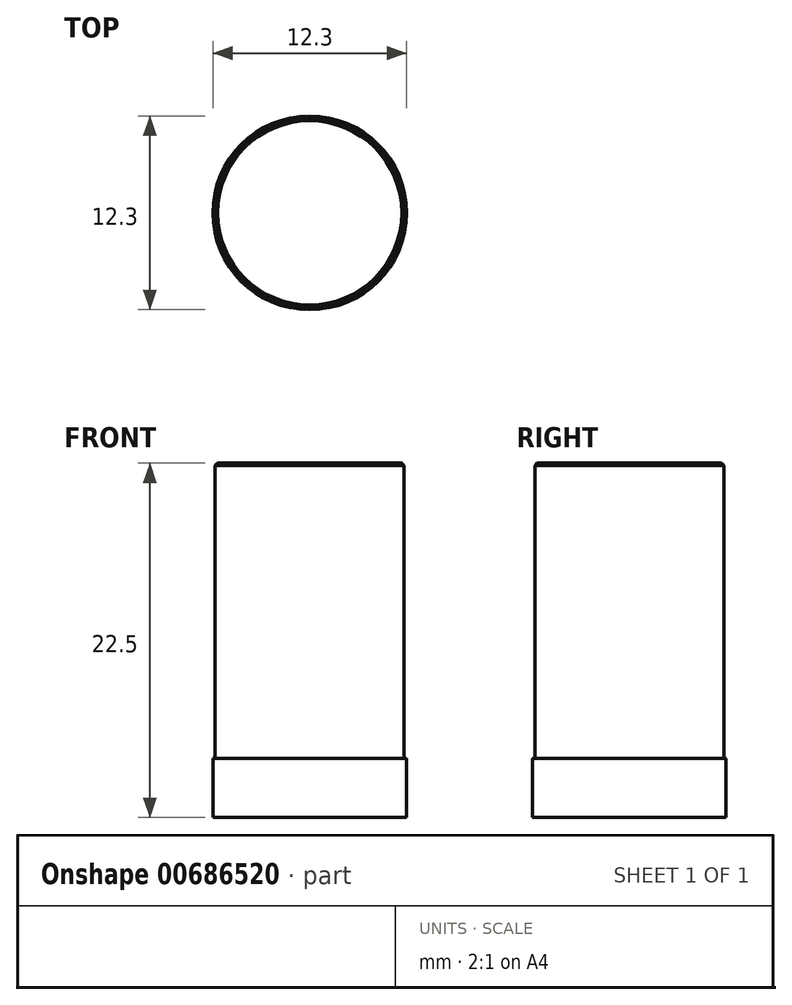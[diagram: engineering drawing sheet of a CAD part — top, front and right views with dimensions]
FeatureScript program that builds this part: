
annotation { "Feature Type Name" : "Feature", "Feature Type Description" : "" }
export const myFeature = defineFeature(function(context is Context, id is Id, definition is map)
    precondition{}
    {
        {
            var Q0;
            Q0=qCreatedBy(makeId("Top.planeOp"),FACE);
            var sketch = newSketch(context, id + "F0", { "sketchPlane" : qUnion([Q0])});
            skCircle(sketch, "E0", {"center": v(0, 0) * mm, "radius": 6 * mm});
            skSolve(sketch);
        }
        {
            var Q0;
            Q0=makeQuery(id+"F0.imprint","IMPRINT",FACE,{"disambiguationData":[TD([[makeQuery(id+"F0.imprint","IMPRINT",EDGE,{"derivedFrom":sQuery(id+"F0.wireOp",EDGE,"E0")}),1.0]])]});
            extrude(context, id + "F1", {"entities" : qUnion([Q0]), "depth" : 22.5 * mm, "offsetDistance" : 25 * mm});
        }
        {
            var Q0;
            Q0=qCreatedBy(makeId("Top.planeOp"),FACE);
            var sketch = newSketch(context, id + "F2", { "sketchPlane" : qUnion([Q0])});
            skCircle(sketch, "E1", {"center": v(0, 0) * mm, "radius": 6.15 * mm});
            skSolve(sketch);
        }
        {
            var Q0;
            Q0=makeQuery(id+"F2.imprint","IMPRINT",FACE,{"disambiguationData":[TD([[makeQuery(id+"F2.imprint","IMPRINT",EDGE,{"derivedFrom":sQuery(id+"F2.wireOp",EDGE,"E1")}),1.0]])]});
            extrude(context, id + "F3", {"entities" : qUnion([Q0]), "operationType" : NewBodyOperationType.ADD, "depth" : 3.75 * mm, "offsetDistance" : 25 * mm});
        }
        {
            var Q0;
            Q0=makeQuery(id+"F3.boolean.opBoolean","INTERSECT",EDGE,{"derivedFrom":[makeQuery(id+"F1.opExtrude","SWEPT_FACE",FACE,{"disambiguationData":[OSD([sQuery(id+"F0.wireOp",EDGE,"E0")])]}),makeQuery(id+"F3.opExtrude","CAP_FACE",FACE,{"disambiguationData":[OSD([sQuery(id+"F2.wireOp",EDGE,"E1")])],"isStart":false})]});
            fillet(context, id + "F4", {"entities" : qUnion([Q0]), "radius" : .15 * mm, "tangentPropagation" : true, "allowEdgeOverflow" : false});
        }
        {
            var Q0;
            Q0=makeQuery(id+"F1.opExtrude","CAP_EDGE",EDGE,{"disambiguationData":[OSD([sQuery(id+"F0.wireOp",EDGE,"E0")])],"isStart":false});
            chamfer(context, id + "F5", {"entities" : qUnion([Q0]), "chamferType" : ChamferType.OFFSET_ANGLE, "width" : .15 * mm, "oppositeDirection" : false, "angle" : 45 * degree, "tangentPropagation" : true});
        }
    });
